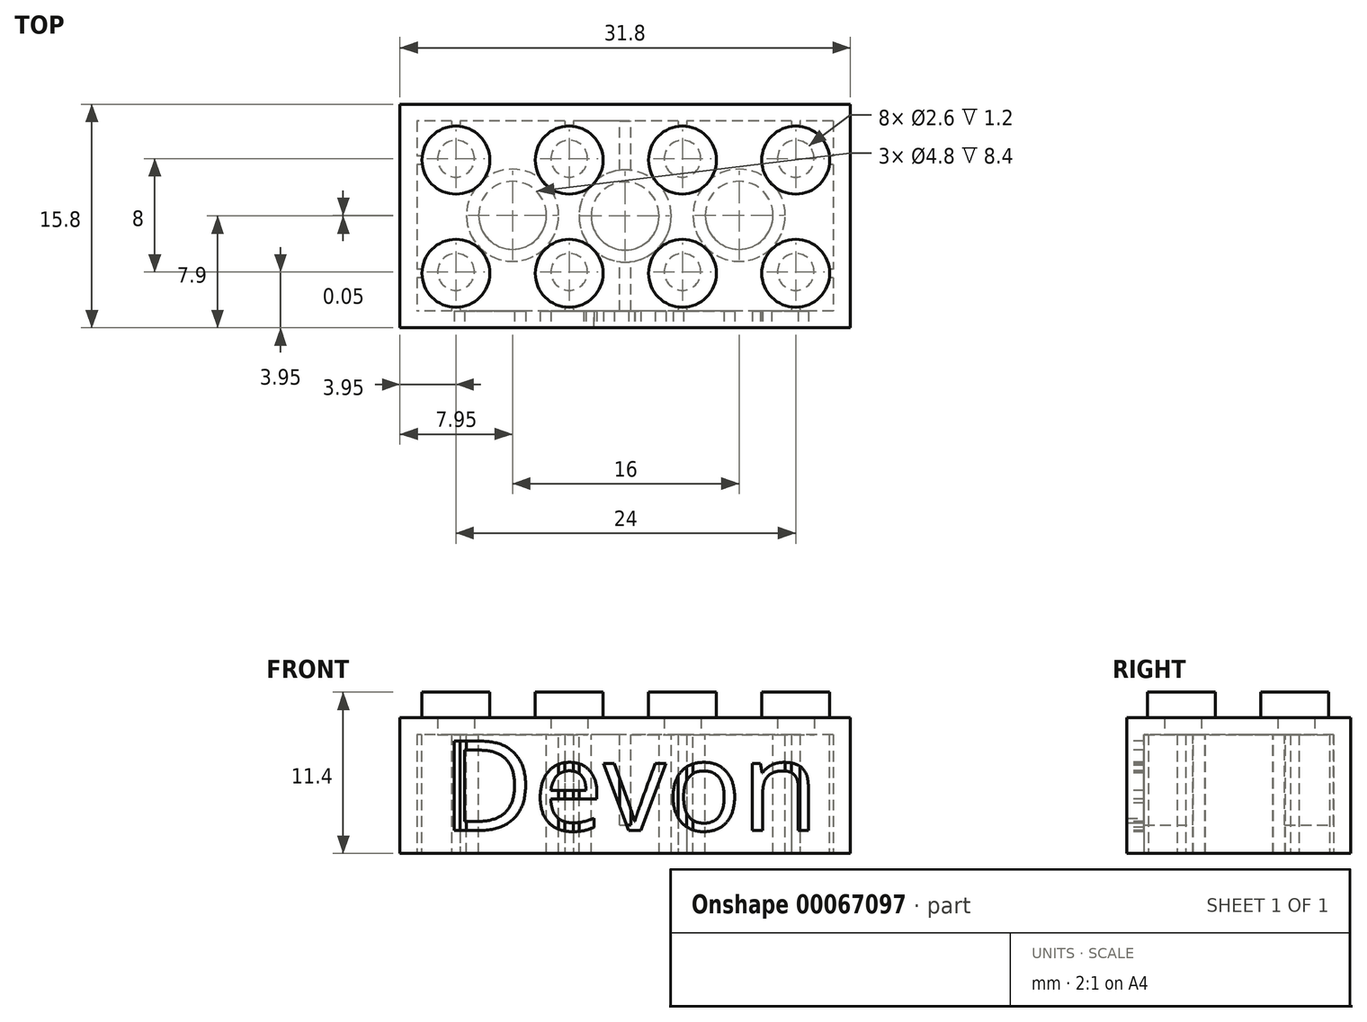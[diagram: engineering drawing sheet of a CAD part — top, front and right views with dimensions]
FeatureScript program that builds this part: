
annotation { "Feature Type Name" : "Feature", "Feature Type Description" : "" }
export const myFeature = defineFeature(function(context is Context, id is Id, definition is map)
    precondition{}
    {
        {
            var Q0;
            Q0=qCreatedBy(makeId("Top.planeOp"),FACE);
            var sketch = newSketch(context, id + "F0", { "sketchPlane" : qUnion([Q0])});
            skLineSegment(sketch, "E0.rect.bottom", {"start": v(-15.9, 7.9) * mm, "end": v(15.9, 7.9) * mm});
            skLineSegment(sketch, "E0.rect.top", {"start": v(-15.9, -7.9) * mm, "end": v(15.9, -7.9) * mm});
            skLineSegment(sketch, "E0.rect.left", {"start": v(-15.9, 7.9) * mm, "end": v(-15.9, -7.9) * mm});
            skLineSegment(sketch, "E0.rect.right", {"start": v(15.9, 7.9) * mm, "end": v(15.9, -7.9) * mm});
            skPoint(sketch, "E0.rect.middle", {"position": v(0, 0) * mm});
            skSolve(sketch);
        }
        {
            var Q0;
            Q0 = qSketchRegion(id + "F0", true);
            extrude(context, id + "F1", {"entities" : qUnion([Q0]), "depth" : 9.6 * mm});
        }
        {
            var Q0;
            Q0=makeQuery(id+"F1.opExtrude","CAP_FACE",FACE,{"disambiguationData":[OSD([sQuery(id+"F0.wireOp",EDGE,"E0.rect.bottom"),sQuery(id+"F0.wireOp",EDGE,"E0.rect.top"),sQuery(id+"F0.wireOp",EDGE,"E0.rect.left"),sQuery(id+"F0.wireOp",EDGE,"E0.rect.right")])],"isStart":true});
            var sketch = newSketch(context, id + "F2", { "sketchPlane" : qUnion([Q0])});
            skLineSegment(sketch, "E1.rect.bottom", {"start": v(14.7, -6.7) * mm, "end": v(-14.7, -6.7) * mm});
            skLineSegment(sketch, "E1.rect.top", {"start": v(14.7, 6.7) * mm, "end": v(-14.7, 6.7) * mm});
            skLineSegment(sketch, "E1.rect.left", {"start": v(14.7, -6.7) * mm, "end": v(14.7, 6.7) * mm});
            skLineSegment(sketch, "E1.rect.right", {"start": v(-14.7, -6.7) * mm, "end": v(-14.7, 6.7) * mm});
            skPoint(sketch, "E1.rect.middle", {"position": v(0, 0) * mm});
            skSolve(sketch);
        }
        {
            var Q0;
            Q0 = qSketchRegion(id + "F2", true);
            extrude(context, id + "F3", {"entities" : qUnion([Q0]), "operationType" : NewBodyOperationType.REMOVE, "oppositeDirection" : true, "depth" : 8.4 * mm});
        }
        {
            var Q0;
            Q0=makeQuery(id+"F1.opExtrude","CAP_FACE",FACE,{"disambiguationData":[OSD([sQuery(id+"F0.wireOp",EDGE,"E0.rect.bottom"),sQuery(id+"F0.wireOp",EDGE,"E0.rect.top"),sQuery(id+"F0.wireOp",EDGE,"E0.rect.left"),sQuery(id+"F0.wireOp",EDGE,"E0.rect.right")])],"isStart":false});
            var sketch = newSketch(context, id + "F4", { "sketchPlane" : qUnion([Q0])});
            skLineSegment(sketch, "E2", {"start": v(-28.6, 0) * mm, "end": v(26.98, 0) * mm, "construction": true});
            skCircle(sketch, "E3", {"center": v(-11.95, 3.95) * mm, "radius": 2.4 * mm});
            skCircle(sketch, "E4.0.1.0", {"center": v(-11.95, -4.05) * mm, "radius": 2.4 * mm});
            skCircle(sketch, "E4.1.0.0", {"center": v(-3.95, 3.95) * mm, "radius": 2.4 * mm});
            skCircle(sketch, "E4.1.1.0", {"center": v(-3.95, -4.05) * mm, "radius": 2.4 * mm});
            skCircle(sketch, "E4.2.0.0", {"center": v(4.05, 3.95) * mm, "radius": 2.4 * mm});
            skCircle(sketch, "E4.2.1.0", {"center": v(4.05, -4.05) * mm, "radius": 2.4 * mm});
            skCircle(sketch, "E4.3.0.0", {"center": v(12.05, 3.95) * mm, "radius": 2.4 * mm});
            skCircle(sketch, "E4.3.1.0", {"center": v(12.05, -4.05) * mm, "radius": 2.4 * mm});
            skLineSegment(sketch, "E4.direction1", {"start": v(-11.95, 3.95) * mm, "end": v(-3.95, 3.95) * mm, "construction": true});
            skLineSegment(sketch, "E4.direction2", {"start": v(-11.95, 3.95) * mm, "end": v(-11.95, -4.05) * mm, "construction": true});
            skSolve(sketch);
        }
        {
            var Q0;
            Q0 = qSketchRegion(id + "F4", true);
            extrude(context, id + "F5", {"entities" : qUnion([Q0]), "operationType" : NewBodyOperationType.ADD, "depth" : 1.8 * mm});
        }
        {
            var Q0;
            Q0=makeQuery(id+"F3.boolean.opBoolean","COPY",FACE,{"derivedFrom":makeQuery(id+"F3.opExtrude","CAP_FACE",FACE,{"disambiguationData":[OSD([sQuery(id+"F2.wireOp",EDGE,"E1.rect.bottom"),sQuery(id+"F2.wireOp",EDGE,"E1.rect.top"),sQuery(id+"F2.wireOp",EDGE,"E1.rect.left"),sQuery(id+"F2.wireOp",EDGE,"E1.rect.right")])],"isStart":false})});
            var sketch = newSketch(context, id + "F6", { "sketchPlane" : qUnion([Q0])});
            skCircle(sketch, "E5", {"center": v(-11.95, 3.95) * mm, "radius": 1.3 * mm});
            skCircle(sketch, "E6.0.1.0", {"center": v(-11.95, -4.05) * mm, "radius": 1.3 * mm});
            skCircle(sketch, "E6.1.0.0", {"center": v(-3.95, 3.95) * mm, "radius": 1.3 * mm});
            skCircle(sketch, "E6.1.1.0", {"center": v(-3.95, -4.05) * mm, "radius": 1.3 * mm});
            skCircle(sketch, "E6.2.0.0", {"center": v(4.05, 3.95) * mm, "radius": 1.3 * mm});
            skCircle(sketch, "E6.2.1.0", {"center": v(4.05, -4.05) * mm, "radius": 1.3 * mm});
            skCircle(sketch, "E6.3.0.0", {"center": v(12.05, 3.95) * mm, "radius": 1.3 * mm});
            skCircle(sketch, "E6.3.1.0", {"center": v(12.05, -4.05) * mm, "radius": 1.3 * mm});
            skLineSegment(sketch, "E6.direction1", {"start": v(-11.95, 3.95) * mm, "end": v(-3.95, 3.95) * mm, "construction": true});
            skLineSegment(sketch, "E6.direction2", {"start": v(-11.95, 3.95) * mm, "end": v(-11.95, -4.05) * mm, "construction": true});
            skSolve(sketch);
        }
        {
            var Q0;
            Q0 = qSketchRegion(id + "F6", true);
            extrude(context, id + "F7", {"entities" : qUnion([Q0]), "operationType" : NewBodyOperationType.REMOVE, "oppositeDirection" : true, "depth" : 1.2 * mm});
        }
        {
            var Q0;
            Q0=makeQuery(id+"F3.boolean.opBoolean","COPY",FACE,{"derivedFrom":makeQuery(id+"F3.opExtrude","CAP_FACE",FACE,{"disambiguationData":[OSD([sQuery(id+"F2.wireOp",EDGE,"E1.rect.bottom"),sQuery(id+"F2.wireOp",EDGE,"E1.rect.top"),sQuery(id+"F2.wireOp",EDGE,"E1.rect.left"),sQuery(id+"F2.wireOp",EDGE,"E1.rect.right")])],"isStart":false})});
            var sketch = newSketch(context, id + "F8", { "sketchPlane" : qUnion([Q0])});
            skLineSegment(sketch, "E7", {"start": v(-11.95, 3.95) * mm, "end": v(-3.95, -4.05) * mm, "construction": true});
            skLineSegment(sketch, "E8", {"start": v(-3.95, 3.95) * mm, "end": v(-11.95, -4.05) * mm, "construction": true});
            skLineSegment(sketch, "E9", {"start": v(4.05, 3.95) * mm, "end": v(12.05, -4.05) * mm, "construction": true});
            skLineSegment(sketch, "E10", {"start": v(4.05, -4.05) * mm, "end": v(12.05, 3.95) * mm, "construction": true});
            skLineSegment(sketch, "E11", {"start": v(-3.95, 3.95) * mm, "end": v(4.05, -4.05) * mm, "construction": true});
            skLineSegment(sketch, "E12", {"start": v(4.05, 3.95) * mm, "end": v(-3.95, -4.05) * mm, "construction": true});
            skPoint(sketch, "E13", {"position": v(-7.95, -0.05) * mm});
            skPoint(sketch, "E14", {"position": v(8.05, -0.05) * mm});
            skCircle(sketch, "E15", {"center": v(-7.95, -0.05) * mm, "radius": 2.4 * mm});
            skCircle(sketch, "E16", {"center": v(-7.95, -0.05) * mm, "radius": 3.25 * mm});
            skCircle(sketch, "E17", {"center": v(0, 0) * mm, "radius": 2.4 * mm});
            skCircle(sketch, "E18", {"center": v(0, 0) * mm, "radius": 3.25 * mm});
            skCircle(sketch, "E19", {"center": v(8.05, -0.05) * mm, "radius": 2.4 * mm});
            skCircle(sketch, "E20", {"center": v(8.05, -0.05) * mm, "radius": 3.25 * mm});
            skSolve(sketch);
        }
        {
            var Q0;
            Q0 = qSketchRegion(id + "F8", true);
            var Q1;
            Q1=makeQuery(id+"F1.opExtrude","CAP_FACE",FACE,{"disambiguationData":[OSD([sQuery(id+"F0.wireOp",EDGE,"E0.rect.bottom"),sQuery(id+"F0.wireOp",EDGE,"E0.rect.top"),sQuery(id+"F0.wireOp",EDGE,"E0.rect.left"),sQuery(id+"F0.wireOp",EDGE,"E0.rect.right")])],"isStart":true});
            extrude(context, id + "F9", {"entities" : qUnion([Q0]), "operationType" : NewBodyOperationType.ADD, "endBound" : BoundingType.UP_TO_SURFACE, "endBoundEntityFace" : qUnion([Q1]), "depth" : 25 * mm});
        }
        {
            var Q0;
            Q0=makeQuery(id+"F1.opExtrude","CAP_FACE",FACE,{"disambiguationData":[OSD([sQuery(id+"F0.wireOp",EDGE,"E0.rect.bottom"),sQuery(id+"F0.wireOp",EDGE,"E0.rect.top"),sQuery(id+"F0.wireOp",EDGE,"E0.rect.left"),sQuery(id+"F0.wireOp",EDGE,"E0.rect.right")])],"isStart":true});
            var sketch = newSketch(context, id + "F10", { "sketchPlane" : qUnion([Q0])});
            skLineSegment(sketch, "E21.bottom", {"start": v(-12.25, 6.7) * mm, "end": v(-11.65, 6.7) * mm});
            skLineSegment(sketch, "E21.top", {"start": v(-12.25, 6.4) * mm, "end": v(-11.65, 6.4) * mm});
            skLineSegment(sketch, "E21.left", {"start": v(-12.25, 6.7) * mm, "end": v(-12.25, 6.4) * mm});
            skLineSegment(sketch, "E21.right", {"start": v(-11.65, 6.7) * mm, "end": v(-11.65, 6.4) * mm});
            skLineSegment(sketch, "E22", {"start": v(-11.95, 15.64) * mm, "end": v(-11.95, -3.95) * mm, "construction": true});
            skLineSegment(sketch, "E23.0.1.0", {"start": v(-12.25, -6.7) * mm, "end": v(-11.65, -6.7) * mm});
            skLineSegment(sketch, "E23.0.1.1", {"start": v(-12.25, -6.4) * mm, "end": v(-11.65, -6.4) * mm});
            skLineSegment(sketch, "E23.0.1.2", {"start": v(-11.65, -6.4) * mm, "end": v(-11.65, -6.7) * mm});
            skLineSegment(sketch, "E23.0.1.3", {"start": v(-12.25, -6.4) * mm, "end": v(-12.25, -6.7) * mm});
            skLineSegment(sketch, "E23.1.0.0", {"start": v(-4.25, 6.4) * mm, "end": v(-3.65, 6.4) * mm});
            skLineSegment(sketch, "E23.1.0.1", {"start": v(-4.25, 6.7) * mm, "end": v(-3.65, 6.7) * mm});
            skLineSegment(sketch, "E23.1.0.2", {"start": v(-3.65, 6.7) * mm, "end": v(-3.65, 6.4) * mm});
            skLineSegment(sketch, "E23.1.0.3", {"start": v(-4.25, 6.7) * mm, "end": v(-4.25, 6.4) * mm});
            skLineSegment(sketch, "E23.1.1.0", {"start": v(-4.25, -6.7) * mm, "end": v(-3.65, -6.7) * mm});
            skLineSegment(sketch, "E23.1.1.1", {"start": v(-4.25, -6.4) * mm, "end": v(-3.65, -6.4) * mm});
            skLineSegment(sketch, "E23.1.1.2", {"start": v(-3.65, -6.4) * mm, "end": v(-3.65, -6.7) * mm});
            skLineSegment(sketch, "E23.1.1.3", {"start": v(-4.25, -6.4) * mm, "end": v(-4.25, -6.7) * mm});
            skLineSegment(sketch, "E23.2.0.0", {"start": v(3.75, 6.4) * mm, "end": v(4.35, 6.4) * mm});
            skLineSegment(sketch, "E23.2.0.1", {"start": v(3.75, 6.7) * mm, "end": v(4.35, 6.7) * mm});
            skLineSegment(sketch, "E23.2.0.2", {"start": v(4.35, 6.7) * mm, "end": v(4.35, 6.4) * mm});
            skLineSegment(sketch, "E23.2.0.3", {"start": v(3.75, 6.7) * mm, "end": v(3.75, 6.4) * mm});
            skLineSegment(sketch, "E23.2.1.0", {"start": v(3.75, -6.7) * mm, "end": v(4.35, -6.7) * mm});
            skLineSegment(sketch, "E23.2.1.1", {"start": v(3.75, -6.4) * mm, "end": v(4.35, -6.4) * mm});
            skLineSegment(sketch, "E23.2.1.2", {"start": v(4.35, -6.4) * mm, "end": v(4.35, -6.7) * mm});
            skLineSegment(sketch, "E23.2.1.3", {"start": v(3.75, -6.4) * mm, "end": v(3.75, -6.7) * mm});
            skLineSegment(sketch, "E23.3.0.0", {"start": v(11.75, 6.4) * mm, "end": v(12.35, 6.4) * mm});
            skLineSegment(sketch, "E23.3.0.1", {"start": v(11.75, 6.7) * mm, "end": v(12.35, 6.7) * mm});
            skLineSegment(sketch, "E23.3.0.2", {"start": v(12.35, 6.7) * mm, "end": v(12.35, 6.4) * mm});
            skLineSegment(sketch, "E23.3.0.3", {"start": v(11.75, 6.7) * mm, "end": v(11.75, 6.4) * mm});
            skLineSegment(sketch, "E23.3.1.0", {"start": v(11.75, -6.7) * mm, "end": v(12.35, -6.7) * mm});
            skLineSegment(sketch, "E23.3.1.1", {"start": v(11.75, -6.4) * mm, "end": v(12.35, -6.4) * mm});
            skLineSegment(sketch, "E23.3.1.2", {"start": v(12.35, -6.4) * mm, "end": v(12.35, -6.7) * mm});
            skLineSegment(sketch, "E23.3.1.3", {"start": v(11.75, -6.4) * mm, "end": v(11.75, -6.7) * mm});
            skLineSegment(sketch, "E23.direction1", {"start": v(-12.25, 6.4) * mm, "end": v(-4.25, 6.4) * mm, "construction": true});
            skLineSegment(sketch, "E23.direction2", {"start": v(-12.25, 6.4) * mm, "end": v(-12.25, -6.7) * mm, "construction": true});
            skSolve(sketch);
        }
        {
            var Q0;
            Q0 = qSketchRegion(id + "F10", true);
            var Q1;
            {var subQ0=sQuery(id+"F2.wireOp",EDGE,"E1.rect.bottom");var subQ1=sQuery(id+"F2.wireOp",EDGE,"E1.rect.top");var subQ2=sQuery(id+"F2.wireOp",EDGE,"E1.rect.left");var subQ3=sQuery(id+"F2.wireOp",EDGE,"E1.rect.right");Q1=makeQuery(id+"F9.boolean.opBoolean","SPLIT",FACE,{"disambiguationData":[TD([makeQuery(id+"F3.boolean.opBoolean","COPY",FACE,{"derivedFrom":makeQuery(id+"F3.opExtrude","SWEPT_FACE",FACE,{"disambiguationData":[OSD([subQ0])]})})])],"derivedFrom":makeQuery(id+"F3.boolean.opBoolean","COPY",FACE,{"derivedFrom":makeQuery(id+"F3.opExtrude","CAP_FACE",FACE,{"disambiguationData":[OSD([subQ0,subQ1,subQ2,subQ3])],"isStart":false})})});}
            extrude(context, id + "F11", {"entities" : qUnion([Q0]), "operationType" : NewBodyOperationType.ADD, "endBound" : BoundingType.UP_TO_SURFACE, "oppositeDirection" : true, "endBoundEntityFace" : qUnion([Q1]), "depth" : 25 * mm});
        }
        {
            var Q0;
            Q0=makeQuery(id+"F11.boolean.opBoolean","MERGE",FACE,{"derivedFrom":[makeQuery(id+"F1.opExtrude","CAP_FACE",FACE,{"disambiguationData":[OSD([sQuery(id+"F0.wireOp",EDGE,"E0.rect.bottom"),sQuery(id+"F0.wireOp",EDGE,"E0.rect.top"),sQuery(id+"F0.wireOp",EDGE,"E0.rect.left"),sQuery(id+"F0.wireOp",EDGE,"E0.rect.right")])],"isStart":true}),makeQuery(id+"F11.opExtrude","CAP_FACE",FACE,{"disambiguationData":[OSD([sQuery(id+"F10.wireOp",EDGE,"E21.bottom"),sQuery(id+"F10.wireOp",EDGE,"E21.top"),sQuery(id+"F10.wireOp",EDGE,"E21.left"),sQuery(id+"F10.wireOp",EDGE,"E21.right")])],"isStart":true}),makeQuery(id+"F11.opExtrude","CAP_FACE",FACE,{"disambiguationData":[OSD([sQuery(id+"F10.wireOp",EDGE,"E23.0.1.0"),sQuery(id+"F10.wireOp",EDGE,"E23.0.1.1"),sQuery(id+"F10.wireOp",EDGE,"E23.0.1.2"),sQuery(id+"F10.wireOp",EDGE,"E23.0.1.3")])],"isStart":true}),makeQuery(id+"F11.opExtrude","CAP_FACE",FACE,{"disambiguationData":[OSD([sQuery(id+"F10.wireOp",EDGE,"E23.1.0.0"),sQuery(id+"F10.wireOp",EDGE,"E23.1.0.1"),sQuery(id+"F10.wireOp",EDGE,"E23.1.0.2"),sQuery(id+"F10.wireOp",EDGE,"E23.1.0.3")])],"isStart":true}),makeQuery(id+"F11.opExtrude","CAP_FACE",FACE,{"disambiguationData":[OSD([sQuery(id+"F10.wireOp",EDGE,"E23.1.1.0"),sQuery(id+"F10.wireOp",EDGE,"E23.1.1.1"),sQuery(id+"F10.wireOp",EDGE,"E23.1.1.2"),sQuery(id+"F10.wireOp",EDGE,"E23.1.1.3")])],"isStart":true}),makeQuery(id+"F11.opExtrude","CAP_FACE",FACE,{"disambiguationData":[OSD([sQuery(id+"F10.wireOp",EDGE,"E23.2.0.0"),sQuery(id+"F10.wireOp",EDGE,"E23.2.0.1"),sQuery(id+"F10.wireOp",EDGE,"E23.2.0.2"),sQuery(id+"F10.wireOp",EDGE,"E23.2.0.3")])],"isStart":true}),makeQuery(id+"F11.opExtrude","CAP_FACE",FACE,{"disambiguationData":[OSD([sQuery(id+"F10.wireOp",EDGE,"E23.2.1.0"),sQuery(id+"F10.wireOp",EDGE,"E23.2.1.1"),sQuery(id+"F10.wireOp",EDGE,"E23.2.1.2"),sQuery(id+"F10.wireOp",EDGE,"E23.2.1.3")])],"isStart":true}),makeQuery(id+"F11.opExtrude","CAP_FACE",FACE,{"disambiguationData":[OSD([sQuery(id+"F10.wireOp",EDGE,"E23.3.0.0"),sQuery(id+"F10.wireOp",EDGE,"E23.3.0.1"),sQuery(id+"F10.wireOp",EDGE,"E23.3.0.2"),sQuery(id+"F10.wireOp",EDGE,"E23.3.0.3")])],"isStart":true}),makeQuery(id+"F11.opExtrude","CAP_FACE",FACE,{"disambiguationData":[OSD([sQuery(id+"F10.wireOp",EDGE,"E23.3.1.0"),sQuery(id+"F10.wireOp",EDGE,"E23.3.1.1"),sQuery(id+"F10.wireOp",EDGE,"E23.3.1.2"),sQuery(id+"F10.wireOp",EDGE,"E23.3.1.3")])],"isStart":true})]});
            var sketch = newSketch(context, id + "F12", { "sketchPlane" : qUnion([Q0])});
            skLineSegment(sketch, "E24", {"start": v(-21.2, 4.05) * mm, "end": v(-11.95, 4.05) * mm, "construction": true});
            skLineSegment(sketch, "E25.bottom", {"start": v(-14.7, 4.35) * mm, "end": v(-14.4, 4.35) * mm});
            skLineSegment(sketch, "E25.top", {"start": v(-14.7, 3.75) * mm, "end": v(-14.4, 3.75) * mm});
            skLineSegment(sketch, "E25.left", {"start": v(-14.7, 4.35) * mm, "end": v(-14.7, 3.75) * mm});
            skLineSegment(sketch, "E25.right", {"start": v(-14.4, 4.35) * mm, "end": v(-14.4, 3.75) * mm});
            skLineSegment(sketch, "E26.0.1.0", {"start": v(-14.7, -4.25) * mm, "end": v(-14.4, -4.25) * mm});
            skLineSegment(sketch, "E26.0.1.1", {"start": v(-14.7, -3.65) * mm, "end": v(-14.7, -4.25) * mm});
            skLineSegment(sketch, "E26.0.1.2", {"start": v(-14.7, -3.65) * mm, "end": v(-14.4, -3.65) * mm});
            skLineSegment(sketch, "E26.0.1.3", {"start": v(-14.4, -3.65) * mm, "end": v(-14.4, -4.25) * mm});
            skLineSegment(sketch, "E26.1.0.0", {"start": v(14.4, 3.75) * mm, "end": v(14.7, 3.75) * mm});
            skLineSegment(sketch, "E26.1.0.1", {"start": v(14.4, 4.35) * mm, "end": v(14.4, 3.75) * mm});
            skLineSegment(sketch, "E26.1.0.2", {"start": v(14.4, 4.35) * mm, "end": v(14.7, 4.35) * mm});
            skLineSegment(sketch, "E26.1.0.3", {"start": v(14.7, 4.35) * mm, "end": v(14.7, 3.75) * mm});
            skLineSegment(sketch, "E26.1.1.0", {"start": v(14.4, -4.25) * mm, "end": v(14.7, -4.25) * mm});
            skLineSegment(sketch, "E26.1.1.1", {"start": v(14.4, -3.65) * mm, "end": v(14.4, -4.25) * mm});
            skLineSegment(sketch, "E26.1.1.2", {"start": v(14.4, -3.65) * mm, "end": v(14.7, -3.65) * mm});
            skLineSegment(sketch, "E26.1.1.3", {"start": v(14.7, -3.65) * mm, "end": v(14.7, -4.25) * mm});
            skLineSegment(sketch, "E26.direction1", {"start": v(-14.7, 3.75) * mm, "end": v(14.4, 3.75) * mm, "construction": true});
            skLineSegment(sketch, "E26.direction2", {"start": v(-14.7, 3.75) * mm, "end": v(-14.7, -4.25) * mm, "construction": true});
            skSolve(sketch);
        }
        {
            var Q0;
            Q0 = qSketchRegion(id + "F12", true);
            var Q1;
            {var subQ0=sQuery(id+"F2.wireOp",EDGE,"E1.rect.bottom");var subQ1=sQuery(id+"F2.wireOp",EDGE,"E1.rect.top");var subQ2=sQuery(id+"F2.wireOp",EDGE,"E1.rect.left");var subQ3=sQuery(id+"F2.wireOp",EDGE,"E1.rect.right");Q1=makeQuery(id+"F9.boolean.opBoolean","SPLIT",FACE,{"disambiguationData":[TD([makeQuery(id+"F3.boolean.opBoolean","COPY",FACE,{"derivedFrom":makeQuery(id+"F3.opExtrude","SWEPT_FACE",FACE,{"disambiguationData":[OSD([subQ0])]})})])],"derivedFrom":makeQuery(id+"F3.boolean.opBoolean","COPY",FACE,{"derivedFrom":makeQuery(id+"F3.opExtrude","CAP_FACE",FACE,{"disambiguationData":[OSD([subQ0,subQ1,subQ2,subQ3])],"isStart":false})})});}
            extrude(context, id + "F13", {"entities" : qUnion([Q0]), "operationType" : NewBodyOperationType.ADD, "endBound" : BoundingType.UP_TO_SURFACE, "oppositeDirection" : true, "endBoundEntityFace" : qUnion([Q1]), "depth" : 25 * mm});
        }
        {
            var Q0;
            {var subQ0=sQuery(id+"F2.wireOp",EDGE,"E1.rect.bottom");var subQ1=sQuery(id+"F2.wireOp",EDGE,"E1.rect.top");var subQ2=sQuery(id+"F2.wireOp",EDGE,"E1.rect.left");var subQ3=sQuery(id+"F2.wireOp",EDGE,"E1.rect.right");Q0=makeQuery(id+"F9.boolean.opBoolean","SPLIT",FACE,{"disambiguationData":[TD([makeQuery(id+"F3.boolean.opBoolean","COPY",FACE,{"derivedFrom":makeQuery(id+"F3.opExtrude","SWEPT_FACE",FACE,{"disambiguationData":[OSD([subQ0])]})})])],"derivedFrom":makeQuery(id+"F3.boolean.opBoolean","COPY",FACE,{"derivedFrom":makeQuery(id+"F3.opExtrude","CAP_FACE",FACE,{"disambiguationData":[OSD([subQ0,subQ1,subQ2,subQ3])],"isStart":false})})});}
            var sketch = newSketch(context, id + "F14", { "sketchPlane" : qUnion([Q0])});
            skLineSegment(sketch, "E27.bottom", {"start": v(-0.4, 6.9) * mm, "end": v(0.4, 6.9) * mm});
            skLineSegment(sketch, "E27.top", {"start": v(-0.4, 3.1) * mm, "end": v(0.4, 3.1) * mm});
            skLineSegment(sketch, "E27.left", {"start": v(-0.4, 6.9) * mm, "end": v(-0.4, 3.1) * mm});
            skLineSegment(sketch, "E27.right", {"start": v(0.4, 6.9) * mm, "end": v(0.4, 3.1) * mm});
            skLineSegment(sketch, "E28.bottom", {"start": v(-0.4, -3.1) * mm, "end": v(0.4, -3.1) * mm});
            skLineSegment(sketch, "E28.top", {"start": v(-0.4, -6.9) * mm, "end": v(0.4, -6.9) * mm});
            skLineSegment(sketch, "E28.left", {"start": v(-0.4, -3.1) * mm, "end": v(-0.4, -6.9) * mm});
            skLineSegment(sketch, "E28.right", {"start": v(0.4, -3.1) * mm, "end": v(0.4, -6.9) * mm});
            skSolve(sketch);
        }
        {
            var Q0;
            Q0 = qSketchRegion(id + "F14", true);
            var Q1;
            Q1=makeQuery(id+"F13.boolean.opBoolean","MERGE",FACE,{"derivedFrom":[makeQuery(id+"F11.boolean.opBoolean","MERGE",FACE,{"derivedFrom":[makeQuery(id+"F1.opExtrude","CAP_FACE",FACE,{"disambiguationData":[OSD([sQuery(id+"F0.wireOp",EDGE,"E0.rect.bottom"),sQuery(id+"F0.wireOp",EDGE,"E0.rect.top"),sQuery(id+"F0.wireOp",EDGE,"E0.rect.left"),sQuery(id+"F0.wireOp",EDGE,"E0.rect.right")])],"isStart":true}),makeQuery(id+"F11.opExtrude","CAP_FACE",FACE,{"disambiguationData":[OSD([sQuery(id+"F10.wireOp",EDGE,"E21.bottom"),sQuery(id+"F10.wireOp",EDGE,"E21.top"),sQuery(id+"F10.wireOp",EDGE,"E21.left"),sQuery(id+"F10.wireOp",EDGE,"E21.right")])],"isStart":true}),makeQuery(id+"F11.opExtrude","CAP_FACE",FACE,{"disambiguationData":[OSD([sQuery(id+"F10.wireOp",EDGE,"E23.0.1.0"),sQuery(id+"F10.wireOp",EDGE,"E23.0.1.1"),sQuery(id+"F10.wireOp",EDGE,"E23.0.1.2"),sQuery(id+"F10.wireOp",EDGE,"E23.0.1.3")])],"isStart":true}),makeQuery(id+"F11.opExtrude","CAP_FACE",FACE,{"disambiguationData":[OSD([sQuery(id+"F10.wireOp",EDGE,"E23.1.0.0"),sQuery(id+"F10.wireOp",EDGE,"E23.1.0.1"),sQuery(id+"F10.wireOp",EDGE,"E23.1.0.2"),sQuery(id+"F10.wireOp",EDGE,"E23.1.0.3")])],"isStart":true}),makeQuery(id+"F11.opExtrude","CAP_FACE",FACE,{"disambiguationData":[OSD([sQuery(id+"F10.wireOp",EDGE,"E23.1.1.0"),sQuery(id+"F10.wireOp",EDGE,"E23.1.1.1"),sQuery(id+"F10.wireOp",EDGE,"E23.1.1.2"),sQuery(id+"F10.wireOp",EDGE,"E23.1.1.3")])],"isStart":true}),makeQuery(id+"F11.opExtrude","CAP_FACE",FACE,{"disambiguationData":[OSD([sQuery(id+"F10.wireOp",EDGE,"E23.2.0.0"),sQuery(id+"F10.wireOp",EDGE,"E23.2.0.1"),sQuery(id+"F10.wireOp",EDGE,"E23.2.0.2"),sQuery(id+"F10.wireOp",EDGE,"E23.2.0.3")])],"isStart":true}),makeQuery(id+"F11.opExtrude","CAP_FACE",FACE,{"disambiguationData":[OSD([sQuery(id+"F10.wireOp",EDGE,"E23.2.1.0"),sQuery(id+"F10.wireOp",EDGE,"E23.2.1.1"),sQuery(id+"F10.wireOp",EDGE,"E23.2.1.2"),sQuery(id+"F10.wireOp",EDGE,"E23.2.1.3")])],"isStart":true}),makeQuery(id+"F11.opExtrude","CAP_FACE",FACE,{"disambiguationData":[OSD([sQuery(id+"F10.wireOp",EDGE,"E23.3.0.0"),sQuery(id+"F10.wireOp",EDGE,"E23.3.0.1"),sQuery(id+"F10.wireOp",EDGE,"E23.3.0.2"),sQuery(id+"F10.wireOp",EDGE,"E23.3.0.3")])],"isStart":true}),makeQuery(id+"F11.opExtrude","CAP_FACE",FACE,{"disambiguationData":[OSD([sQuery(id+"F10.wireOp",EDGE,"E23.3.1.0"),sQuery(id+"F10.wireOp",EDGE,"E23.3.1.1"),sQuery(id+"F10.wireOp",EDGE,"E23.3.1.2"),sQuery(id+"F10.wireOp",EDGE,"E23.3.1.3")])],"isStart":true})]}),makeQuery(id+"F13.opExtrude","CAP_FACE",FACE,{"disambiguationData":[OSD([sQuery(id+"F12.wireOp",EDGE,"E25.bottom"),sQuery(id+"F12.wireOp",EDGE,"E25.top"),sQuery(id+"F12.wireOp",EDGE,"E25.left"),sQuery(id+"F12.wireOp",EDGE,"E25.right")])],"isStart":true}),makeQuery(id+"F13.opExtrude","CAP_FACE",FACE,{"disambiguationData":[OSD([sQuery(id+"F12.wireOp",EDGE,"E26.0.1.0"),sQuery(id+"F12.wireOp",EDGE,"E26.0.1.1"),sQuery(id+"F12.wireOp",EDGE,"E26.0.1.2"),sQuery(id+"F12.wireOp",EDGE,"E26.0.1.3")])],"isStart":true}),makeQuery(id+"F13.opExtrude","CAP_FACE",FACE,{"disambiguationData":[OSD([sQuery(id+"F12.wireOp",EDGE,"E26.1.0.0"),sQuery(id+"F12.wireOp",EDGE,"E26.1.0.1"),sQuery(id+"F12.wireOp",EDGE,"E26.1.0.2"),sQuery(id+"F12.wireOp",EDGE,"E26.1.0.3")])],"isStart":true}),makeQuery(id+"F13.opExtrude","CAP_FACE",FACE,{"disambiguationData":[OSD([sQuery(id+"F12.wireOp",EDGE,"E26.1.1.0"),sQuery(id+"F12.wireOp",EDGE,"E26.1.1.1"),sQuery(id+"F12.wireOp",EDGE,"E26.1.1.2"),sQuery(id+"F12.wireOp",EDGE,"E26.1.1.3")])],"isStart":true})]});
            extrude(context, id + "F15", {"entities" : qUnion([Q0]), "operationType" : NewBodyOperationType.ADD, "endBoundEntityFace" : qUnion([Q1]), "depth" : 6.4 * mm});
        }
        {
            var Q0;
            Q0=makeQuery(id+"F1.opExtrude","SWEPT_FACE",FACE,{"disambiguationData":[OSD([sQuery(id+"F0.wireOp",EDGE,"E0.rect.top")])]});
            var sketch = newSketch(context, id + "F16", { "sketchPlane" : qUnion([Q0])});
            skText(sketch, "E29", { "text": "Devon", "fontName": "OpenSans-Regular.ttf"});
            const initialGuessF16  = {"E29": [-0.01293, 0.00163, 1, 0, 0.00636]};
            skSetInitialGuess(sketch, initialGuessF16);
            skSolve(sketch);
        }
        {
            var Q0;
            Q0 = qSketchRegion(id + "F16", true);
            extrude(context, id + "F17", {"entities" : qUnion([Q0]), "operationType" : NewBodyOperationType.REMOVE, "oppositeDirection" : true, "depth" : 1.2 * mm});
        }
    });
